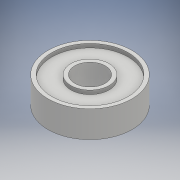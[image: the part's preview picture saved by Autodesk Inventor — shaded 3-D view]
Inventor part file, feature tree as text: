
AUTODESK INVENTOR PART (.ipt)
format: ipt  version: 2017 (Build 210142000, 142)  size: 133,120 bytes
history: native  units: mm
features: extrude x3, sketch x3, other x1
ambient origin geometry x8: Origin, YZ Plane, XZ Plane, XY Plane, X Axis, Y Axis, Z Axis, Center Point
bodies: Body1 (feature_tree)
feature tree (7):
  other  "Твердое тело1"
  extrude  "Выдавливание1"  Depth=8.0mm
  extrude  "Выдавливание3"  Depth=22.0mm
  extrude  "Выдавливание4"  Depth=7.0mm TaperAngle=0.0deg
  sketch  "Эскиз1"
  sketch  "Эскиз3"
  sketch  "Эскиз4"
